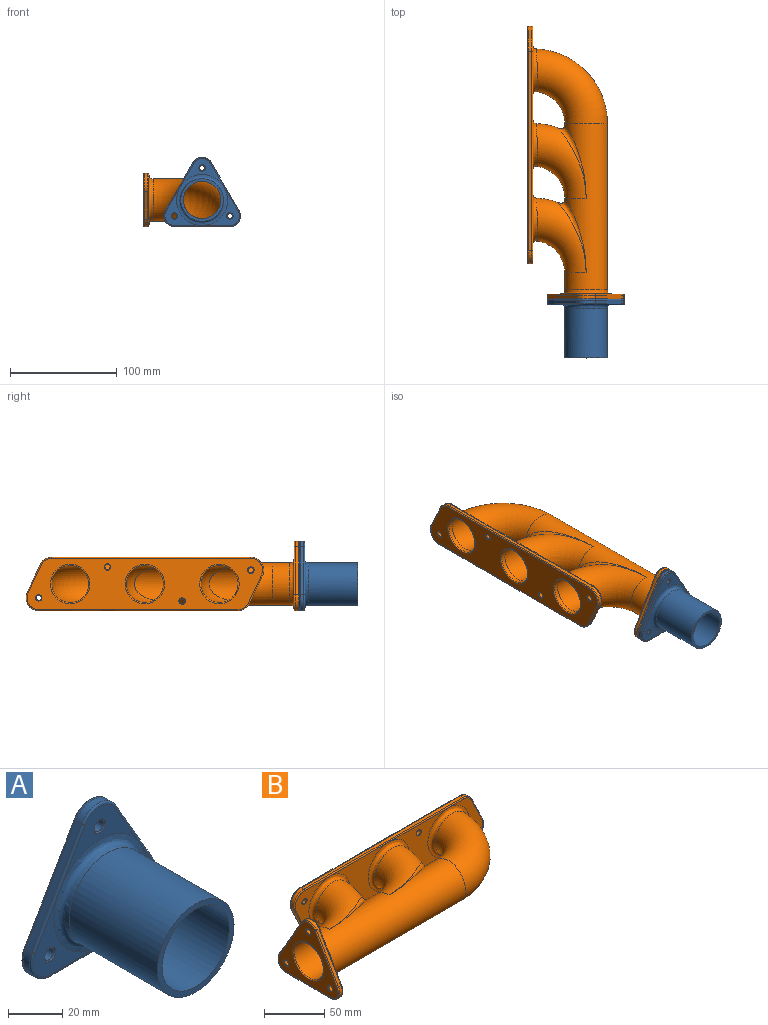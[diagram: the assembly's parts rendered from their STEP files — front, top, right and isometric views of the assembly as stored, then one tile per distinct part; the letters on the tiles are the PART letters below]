
ASSEMBLY  parts=2 mates=1
PART A: 36 faces, bbox 72x55x65 mm
  f0: plane 36.01x34.99mm, normal (0,-1,0), area 310.6mm2, adj f16,f18,f20,f29,f33
  f1: plane 41.59x27.02mm, normal (0,-1,0), area 310.7mm2, adj f19,f20,f21,f29,f35
  f2: plane 45x25.98mm, normal (-0.87,0,0.5), area 155.9mm2, adj f13,f15,f20,f25
  f3: plane 51.96x3mm, normal (0,0,-1), area 155.9mm2, adj f13,f14,f16,f22
  f4: plane 45x25.98mm, normal (0.87,0,0.5), area 155.9mm2, adj f14,f15,f19,f26
  f5: cylinder r=2.5mm len=5mm, axis (0,-1,0), area 62.8mm2, adj f34,f35
  f6: cylinder r=2.5mm len=5mm, axis (0,-1,0), area 62.8mm2, adj f30,f31
  f7: cylinder r=2.5mm len=5mm, axis (0,-1,0), area 62.8mm2, adj f32,f33
  f8: cylinder r=17.5mm len=54mm, axis (0,-1,0), area 5937.6mm2, adj f12,f28
  f9: plane 69.97x63.01mm, normal (0,1,0), area 1666.4mm2, adj f22,f23,f24,f25,f26,f27,f28,f30
  f10: plane 36.01x34.99mm, normal (0,-1,0), area 310.8mm2, adj f16,f17,f19,f29,f31
  f11: cylinder r=20mm len=46mm, axis (0,1,0), area 5780.5mm2, adj f12,f29
  f12: plane 40x40mm, normal (0,-1,0), area 294.5mm2, adj f8,f11
  f13: cylinder r=10mm len=15mm, axis (0,-1,0), area 62.8mm2, adj f2,f3,f18,f23
  f14: cylinder r=10mm len=15mm, axis (0,-1,0), area 62.8mm2, adj f3,f4,f17,f24
  f15: cylinder r=10mm len=17.32mm, axis (0,-1,0), area 62.8mm2, adj f2,f4,f21,f27
  f16: bspline ~51.96x1mm, area 91.5mm2, adj f0,f3,f10,f17,f18
  f17: bspline ~15x10mm, area 35.8mm2, adj f10,f14,f16,f19
  f18: bspline ~15x10mm, area 35.8mm2, adj f0,f13,f16,f20
  f19: bspline ~45.5x26.85mm, area 91.5mm2, adj f1,f4,f10,f17,f21
  f20: bspline ~45.5x26.85mm, area 91.5mm2, adj f0,f1,f2,f18,f21
  f21: bspline ~17.32x5.5mm, area 35.8mm2, adj f1,f15,f19,f20
  f22: bspline ~51.96x1mm, area 91.5mm2, adj f3,f9,f23,f24
  f23: bspline ~15x10mm, area 35.8mm2, adj f9,f13,f22,f25
  f24: bspline ~15x10mm, area 35.8mm2, adj f9,f14,f22,f26
  f25: bspline ~45.5x26.85mm, area 91.5mm2, adj f2,f9,f23,f27
  f26: bspline ~45.5x26.85mm, area 91.5mm2, adj f4,f9,f24,f27
  f27: bspline ~17.32x5.5mm, area 35.8mm2, adj f9,f15,f25,f26
  f28: bspline ~37x37mm, area 196.9mm2, adj f8,f9
  f29: bspline ~47.98x47.95mm, area 903.4mm2, adj f0,f1,f10,f11
  f30: cone r=3mm half-angle=45deg, axis (0,1,0), area 12.2mm2, adj f6,f9
  f31: cone r=2.5mm half-angle=45deg, axis (0,-1,0), area 12.2mm2, adj f6,f10
  f32: cone r=3mm half-angle=45deg, axis (0,1,0), area 12.2mm2, adj f7,f9
  f33: cone r=2.5mm half-angle=45deg, axis (0,-1,0), area 12.2mm2, adj f0,f7
  f34: cone r=3mm half-angle=45deg, axis (0,1,0), area 12.2mm2, adj f5,f9
  f35: cone r=2.5mm half-angle=45deg, axis (0,-1,0), area 12.2mm2, adj f1,f5
PART B: 99 faces, bbox 256.6x98.8x65 mm
  f0: plane 70.02x48.01mm, normal (0,-1,0), area 1514.9mm2, adj f1,f95,f96,f97,f98
  f1: bspline ~48.17x47.96mm, area 920.5mm2, adj f0,f2,f94
  f2: plane 70.02x48.01mm, normal (0,-1,0), area 1514.9mm2, adj f1,f3,f93,f95,f97
  f3: bspline ~48.17x47.96mm, area 920.5mm2, adj f2,f4,f92
  f4: plane 48.01x40.37mm, normal (0,-1,0), area 684mm2, adj f3,f5,f89,f90,f91,f95,f97
  f5: bspline ~10.88x7.35mm, area 23.4mm2, adj f4,f6,f89,f97
  f6: cylinder r=12mm len=10.88mm, axis (0,-1,0), area 40.8mm2, adj f5,f7,f87,f88
  f7: bspline ~10.88x7.35mm, area 23.4mm2, adj f6,f8,f85,f86
  f8: plane 221.04x48.01mm, normal (0,1,0), area 6640.1mm2, adj f7,f9,f60,f61,f62,f74,f75,f76
  f9: bspline ~37x37mm, area 196.9mm2, adj f8,f10
  f10: cylinder r=17.5mm len=35mm, axis (0,-1,0), area 439.8mm2, adj f9,f11
  f11: torus R=50mm, axis (0,0,1), area 8635.9mm2, adj f10,f12
  f12: cylinder r=17.5mm len=164mm, axis (1,0,0), area 12931.3mm2, adj f11,f13,f15,f16,f18,f19
  f13: torus R=50mm, axis (0,0,1), area 5681.8mm2, adj f12,f14,f15
  f14: cylinder r=17.5mm len=35mm, axis (0,-1,0), area 439.8mm2, adj f13,f61
  f15: bspline ~60.84x35mm, area 0mm2, adj f12,f13
  f16: torus R=50mm, axis (0,0,1), area 5681.8mm2, adj f12,f17,f18
  f17: cylinder r=17.5mm len=35mm, axis (0,-1,0), area 439.8mm2, adj f16,f60
  f18: bspline ~60.84x35mm, area 0mm2, adj f12,f16
  f19: bspline ~37x37mm, area 196.9mm2, adj f12,f20
  f20: plane 69.97x63.01mm, normal (-1,0,0), area 1666.6mm2, adj f19,f21,f52,f53,f54,f55,f56,f57
  f21: bspline ~15x10mm, area 35.8mm2, adj f20,f22,f52,f56
  f22: cylinder r=10mm len=15mm, axis (1,0,0), area 62.8mm2, adj f21,f23,f50,f51
  f23: plane 45x25.98mm, normal (0,-0.87,0.5), area 155.9mm2, adj f22,f24,f49,f56
  f24: cylinder r=10mm len=17.32mm, axis (1,0,0), area 62.8mm2, adj f23,f25,f48,f55
  f25: plane 45x25.98mm, normal (0,0.87,0.5), area 155.9mm2, adj f24,f26,f47,f54
  f26: cylinder r=10mm len=15mm, axis (1,0,0), area 62.8mm2, adj f25,f27,f51,f53
  f27: bspline ~15x10mm, area 35.8mm2, adj f26,f28,f46,f47
  f28: plane 36.01x34.99mm, normal (1,0,0), area 319.3mm2, adj f27,f29,f30,f46,f47
  f29: cylinder r=2.5mm len=5mm, axis (1,0,0), area 70.7mm2, adj f28,f59
  f30: bspline ~47.98x47.95mm, area 903.4mm2, adj f28,f31,f42,f44
  f31: cylinder r=20mm len=156mm, axis (1,0,0), area 11820.4mm2, adj f30,f32,f35,f38,f39,f40,f92,f94
  f32: bspline ~78.47x62.85mm, area 184.4mm2, adj f31,f33,f92
  f33: bspline ~7.96x7.02mm, area 69.3mm2, adj f32,f34,f92,f94
  f34: bspline ~63.45x26.52mm, area 152.8mm2, adj f33,f40,f92
  f35: bspline ~78.47x62.85mm, area 184.4mm2, adj f31,f36,f94
  f36: bspline ~7.96x7.02mm, area 69.3mm2, adj f35,f37,f38,f94
  f37: bspline ~70.73x26.68mm, area 198.8mm2, adj f36,f39,f94
  f38: torus R=50mm, axis (0,0,1), area 9380.7mm2, adj f31,f36,f39,f96
  f39: cylinder r=20mm len=70mm, axis (1,0,0), area 959.3mm2, adj f31,f37,f38
  f40: cylinder r=20mm len=70mm, axis (1,0,0), area 959.3mm2, adj f31,f34,f41,f94
  f41: bspline ~25.23x3.68mm, area 0.2mm2, adj f40,f92
  f42: plane 36.01x34.99mm, normal (1,0,0), area 319.4mm2, adj f30,f43,f46,f49,f50
  f43: cylinder r=2.5mm len=5mm, axis (1,0,0), area 70.7mm2, adj f42,f58
  f44: plane 41.59x27.02mm, normal (1,0,0), area 319.4mm2, adj f30,f45,f47,f48,f49
  f45: cylinder r=2.5mm len=5mm, axis (1,0,0), area 70.7mm2, adj f44,f57
  f46: bspline ~51.96x1mm, area 91.5mm2, adj f27,f28,f42,f50,f51
  f47: bspline ~45.5x26.85mm, area 91.5mm2, adj f25,f27,f28,f44,f48
  f48: bspline ~17.32x5.5mm, area 35.8mm2, adj f24,f44,f47,f49
  f49: bspline ~45.5x26.85mm, area 91.5mm2, adj f23,f42,f44,f48,f50
  f50: bspline ~15x10mm, area 35.8mm2, adj f22,f42,f46,f49
  f51: plane 51.96x3mm, normal (0,0,-1), area 155.9mm2, adj f22,f26,f46,f52
  f52: bspline ~51.96x1mm, area 91.5mm2, adj f20,f21,f51,f53
  f53: bspline ~15x10mm, area 35.8mm2, adj f20,f26,f52,f54
  f54: bspline ~45.5x26.85mm, area 91.5mm2, adj f20,f25,f53,f55
  f55: bspline ~17.32x5.5mm, area 35.8mm2, adj f20,f24,f54,f56
  f56: bspline ~45.5x26.85mm, area 91.5mm2, adj f20,f21,f23,f55
  f57: cone r=2.5mm half-angle=45deg, axis (-1,0,0), area 12.2mm2, adj f20,f45
  f58: cone r=2.5mm half-angle=45deg, axis (-1,0,0), area 12.2mm2, adj f20,f43
  f59: cone r=2.5mm half-angle=45deg, axis (-1,0,0), area 12.2mm2, adj f20,f29
  f60: bspline ~37x37mm, area 196.9mm2, adj f8,f17
  f61: bspline ~37x37mm, area 196.9mm2, adj f8,f14
  f62: bspline ~17.07x12.11mm, area 41.4mm2, adj f8,f63,f74,f86
  f63: cylinder r=12mm len=17.07mm, axis (0,-1,0), area 72.3mm2, adj f62,f64,f73,f88
  f64: bspline ~17.07x12.11mm, area 41.4mm2, adj f63,f65,f72,f97
  f65: plane 48.01x40.69mm, normal (0,-1,0), area 702mm2, adj f64,f66,f70,f72,f95,f96,f97
  f66: bspline ~10.88x7.35mm, area 23.4mm2, adj f65,f67,f72,f95
  f67: cylinder r=12mm len=10.88mm, axis (0,-1,0), area 40.8mm2, adj f66,f68,f73,f75
  f68: plane 186.83x3mm, normal (0,0,1), area 560.5mm2, adj f67,f69,f76,f95
  f69: cylinder r=12mm len=17.07mm, axis (0,-1,0), area 72.3mm2, adj f68,f77,f87,f90
  f70: cone r=3mm half-angle=45deg, axis (0,-1,0), area 12.2mm2, adj f65,f71
  f71: cylinder r=2.5mm len=5mm, axis (0,-1,0), area 62.8mm2, adj f70,f78
  f72: bspline ~26.42x13.03mm, area 50.5mm2, adj f64,f65,f66,f73
  f73: plane 26x12.12mm, normal (0.91,0,0.42), area 86.1mm2, adj f63,f67,f72,f74
  f74: bspline ~26.42x13.03mm, area 50.5mm2, adj f8,f62,f73,f75
  f75: bspline ~10.88x7.35mm, area 23.4mm2, adj f8,f67,f74,f76
  f76: bspline ~186.83x1mm, area 329.1mm2, adj f8,f68,f75,f77
  f77: bspline ~17.07x12.11mm, area 41.4mm2, adj f8,f69,f76,f85
  f78: cone r=2.5mm half-angle=45deg, axis (0,1,0), area 12.2mm2, adj f8,f71
  f79: cone r=2.5mm half-angle=45deg, axis (0,1,0), area 12.2mm2, adj f8,f80
  f80: cylinder r=2.5mm len=5mm, axis (0,-1,0), area 62.8mm2, adj f79,f98
  f81: cone r=2.5mm half-angle=45deg, axis (0,1,0), area 12.2mm2, adj f8,f82
  f82: cylinder r=2.5mm len=5mm, axis (0,-1,0), area 62.8mm2, adj f81,f93
  f83: cone r=2.5mm half-angle=45deg, axis (0,1,0), area 12.2mm2, adj f8,f84
  f84: cylinder r=2.5mm len=5mm, axis (0,-1,0), area 62.8mm2, adj f83,f91
  f85: bspline ~26.42x13.03mm, area 50.5mm2, adj f7,f8,f77,f87
  f86: bspline ~186.83x1mm, area 329.1mm2, adj f7,f8,f62,f88
  f87: plane 26x12.12mm, normal (-0.91,0,-0.42), area 86.1mm2, adj f6,f69,f85,f89
  f88: plane 186.83x3mm, normal (0,0,-1), area 560.5mm2, adj f6,f63,f86,f97
  f89: bspline ~26.42x13.03mm, area 50.5mm2, adj f4,f5,f87,f90
  f90: bspline ~17.07x12.11mm, area 41.4mm2, adj f4,f69,f89,f95
  f91: cone r=3mm half-angle=45deg, axis (0,-1,0), area 12.2mm2, adj f4,f84
  f92: torus R=50mm, axis (0,0,1), area 5406.6mm2, adj f3,f31,f32,f33,f34,f41
  f93: cone r=3mm half-angle=45deg, axis (0,-1,0), area 12.2mm2, adj f2,f82
  f94: torus R=50mm, axis (0,0,1), area 5406.6mm2, adj f1,f31,f33,f35,f36,f37,f40
  f95: bspline ~186.83x1mm, area 329.1mm2, adj f0,f2,f4,f65,f66,f68,f90
  f96: bspline ~48.17x47.96mm, area 927.5mm2, adj f0,f38,f65
  f97: bspline ~186.83x1mm, area 329.1mm2, adj f0,f2,f4,f5,f64,f65,f88
  f98: cone r=3mm half-angle=45deg, axis (0,-1,0), area 12.2mm2, adj f0,f80
PLACE A t=(-17.55,-2.09,20.32)mm
PLACE B rot(axis=(0,0,1),90deg) t=(-17.55,7.91,20.32)mm
MATE fastened B.f12 <-> A.f8  axis (0,-1,0) through (-17.55,2.91,20.32)mm
